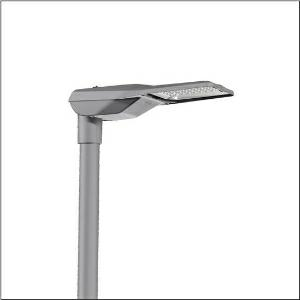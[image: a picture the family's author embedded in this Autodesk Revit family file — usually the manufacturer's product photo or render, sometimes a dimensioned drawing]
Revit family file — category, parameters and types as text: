
# Revit family: streetlight_sl_21_mini___st1_0a_5xe2d33s08gb_0caf
name_source: partatom
category: Lighting Fixtures
units: mm (PartAtom-declared; Revit-internal decimal feet)

## family parameters
Cut with Voids When Loaded = No
Host = Face
Light Source = No
Part Type = Normal
Room Calculation Point = No
Round Connector Dimension = Use Diameter
Shared = No

## types (1)
- --- (1 x LED, 5940 lm, 40.4 W, 3000K)
    Apparent Load = 40 VA
    CIE Flux Codes = 37 72 97 100 100
    Color Rendering = 70
    Color Temperature = 3000K
    Default Elevation = 1800 mm
    Description = Streetlight SL 21 mini, mast luminaire, primary light control with lens, of PMMA, primary optical cover: cover, of toughened safety glass, transparent, light distribution: ST1.0a, light emission: direct distribution, primary light characteristic: asymmetric, installation type: side-entry, post-top, LED, High Power LED, rated luminous flux: 5.940lm, luminous efficacy: 147lm/W, light colour: 730, colour temperature: 3000K, control gear: D4i, control: flexible luminous flux parameterisation, time-dependent luminous flux control, constant luminous flux control, overheat protection, pre-setting: logarithmic dimming characteristic, mains connection: 220..240V, AC, 50/60Hz, start of lifetime: 40W, end of service life: 41W, reduction: 19W, luminaire housing, of diecast aluminium, powder-coated, SITECO metallic grey (DB 702S), corrosivity category C5 high according to DIN EN ISO 12944, please order mast flange separately, inclination adjustable: 0°, 5°, 10°, 15°, sealing non-destructively replaceable, multi-level sealing system, length: 628mm, width: 235mm, height: 110mm, mast flange for spigot size: 42mm (side-entry): 5XC10008XM4, 60/48mm (side-entry/post-top): 5XC10108XM2, 76/60mm (side-entry/post-top): 5XC10108XM1, mounting height: 4..8m, Smart Interface above, protection rating (complete): IP66, insulation class (complete): insulation class II (safety insulation), certification: CE, ENEC, ENEC+, VDE, impact resistance: IK10, permissible operating ambient temperature for outdoor applications: -40..+50°C, standard-compliant lighting for roads and squares, packaging unit: 1 piece

Light Distribution: ST1.0a
    Height = 110 mm
    Lamp = 1 x LED
    Lamp Light Flux = 5940 lm
    Lamp Power = 40.4 W
    Lamp count = 1
    Length = 625 mm
    Luminous efficacy = 147 lm/W
    Manufacturer = Siteco
    ModVariant = No
    Model = 5XE2D33S08GB
    Number of Poles = 1
    OnlyDefault = Yes
    Power Factor = 1
    Product Name = Streetlight SL 21 mini | ST1.0a
    Product group = mast luminaire | pylon top
    ProductGroupID = 6100
    Protection Class = Protection class II
    Protection Degree = IP 66
    RLX_Detail_Level = 1
    RLX_Emergency_Light_Flux = 0 lm
    RLX_Emergency_Type = 0
    RLX_Emergency_Type_DB = No
    RlxData = <blob elided: 26149 chars, md5=8722f487>
    Socket = socket
    Standby Power = 0 W
    System Light Flux = 5940 lm
    System Power = 40 W
    Type Comments = factory setting: luminous flux: 100 % | dim-lin: 254 | 812 mA
    Type Image = l_1003515.jpg
    URL = http://relux.com
    VarID = @adj_186193
    Voltage = 0 V
    Weight = 0.00 kg
    Width = 234 mm

## geometry (parser evidence)
native form markers: Blend x4, Sweep x10
no freeform markers — native parametric forms only
